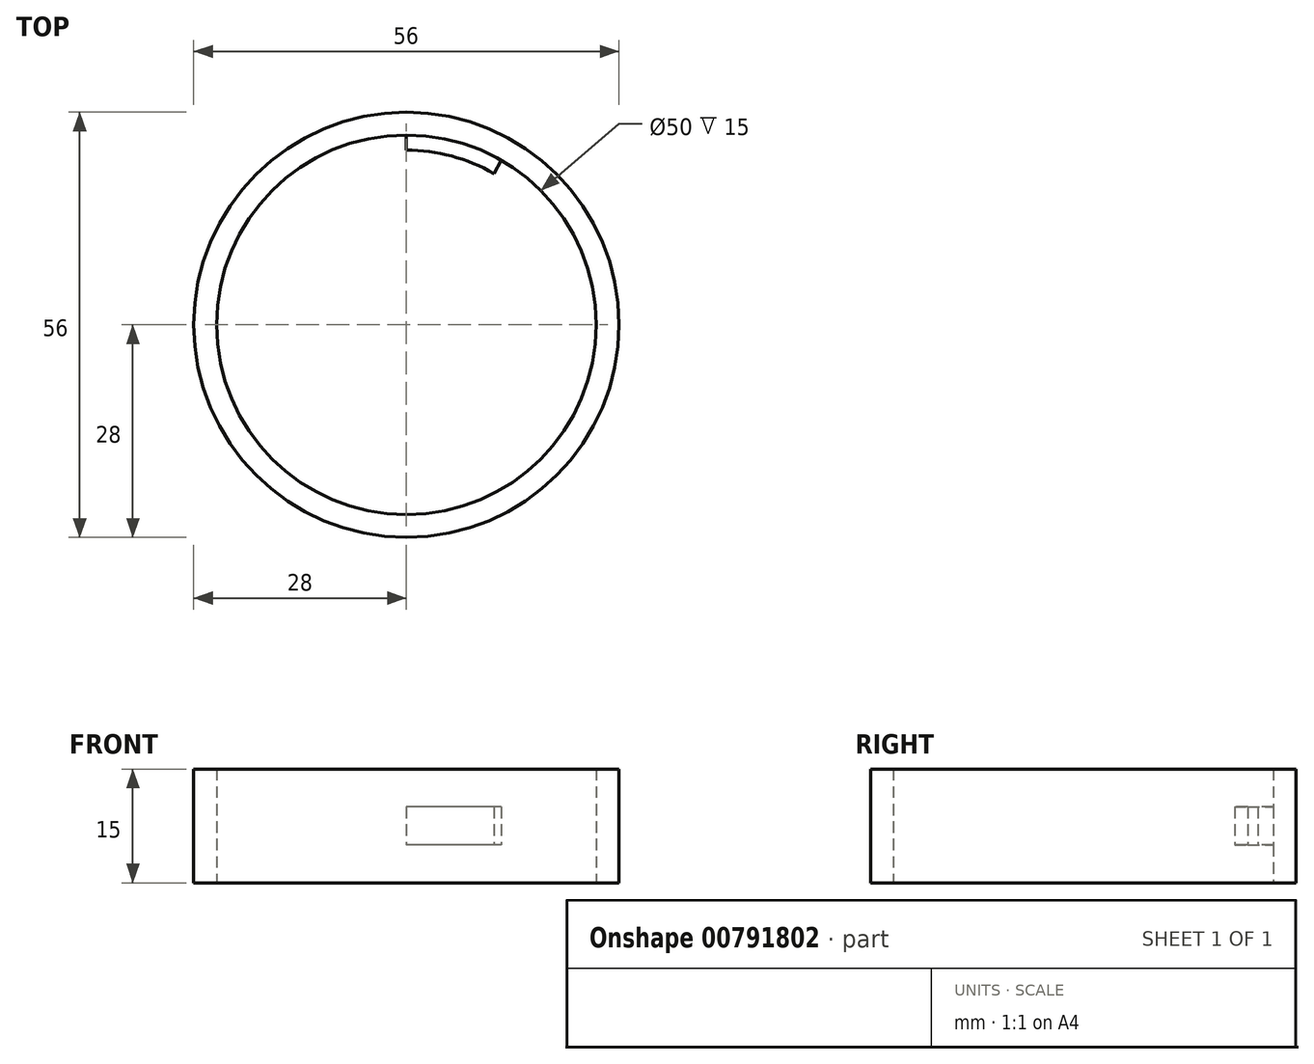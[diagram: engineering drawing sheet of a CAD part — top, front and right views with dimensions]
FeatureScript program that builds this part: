
annotation { "Feature Type Name" : "Feature", "Feature Type Description" : "" }
export const myFeature = defineFeature(function(context is Context, id is Id, definition is map)
    precondition{}
    {
        {
            var Q0;
            Q0=qCreatedBy(makeId("Top.planeOp"),FACE);
            var sketch = newSketch(context, id + "F0", { "sketchPlane" : qUnion([Q0])});
            skCircle(sketch, "E0", {"center": v(0, 0) * mm, "radius": 25 * mm});
            skCircle(sketch, "E1", {"center": v(0, 0) * mm, "radius": 28 * mm});
            skSolve(sketch);
        }
        {
            var Q0;
            Q0 = qSketchRegion(id + "F0", true);
            extrude(context, id + "F1", {"entities" : qUnion([Q0]), "depth" : 15 * mm, "offsetDistance" : 25 * mm});
        }
        {
            var Q0;
            Q0=qCreatedBy(makeId("Top.planeOp"),FACE);
            cPlane(context, id + "F2", {"entities" : qUnion([Q0]), "cplaneType" : CPlaneType.OFFSET, "offset" : 7.5 * mm, "width" : 150 * mm, "height" : 150 * mm});
        }
        {
            var Q0;
            Q0=qCreatedBy(id+"F2.planeOp",FACE);
            var sketch = newSketch(context, id + "F3", { "sketchPlane" : qUnion([Q0])});
            skArc(sketch, "E2", {"start": v(11.5, 19.92) * mm, "mid": v(5.95, 22.22) * mm, "end": v(0, 23) * mm});
            skArc(sketch, "E3.0", {"start": v(12.5, 21.65) * mm, "mid": v(6.47, 24.15) * mm, "end": v(0, 25) * mm});
            skLineSegment(sketch, "E4", {"start": v(0, 25) * mm, "end": v(0, 23) * mm});
            skLineSegment(sketch, "E5", {"start": v(12.5, 21.65) * mm, "end": v(11.5, 19.92) * mm});
            skSolve(sketch);
        }
        {
            var Q0;
            Q0 = qSketchRegion(id + "F3", true);
            var Q1;
            Q1=makeQuery(id+"F1.opExtrude","CAP_FACE",FACE,{"disambiguationData":[OSD([sQuery(id+"F0.wireOp",EDGE,"E0"),sQuery(id+"F0.wireOp",EDGE,"E1")])],"isStart":false});
            extrude(context, id + "F4", {"entities" : qUnion([Q0]), "operationType" : NewBodyOperationType.ADD, "endBound" : BoundingType.SYMMETRIC, "depth" : 5 * mm, "endBoundEntityFace" : qUnion([Q1]), "offsetDistance" : 25 * mm});
        }
    });
